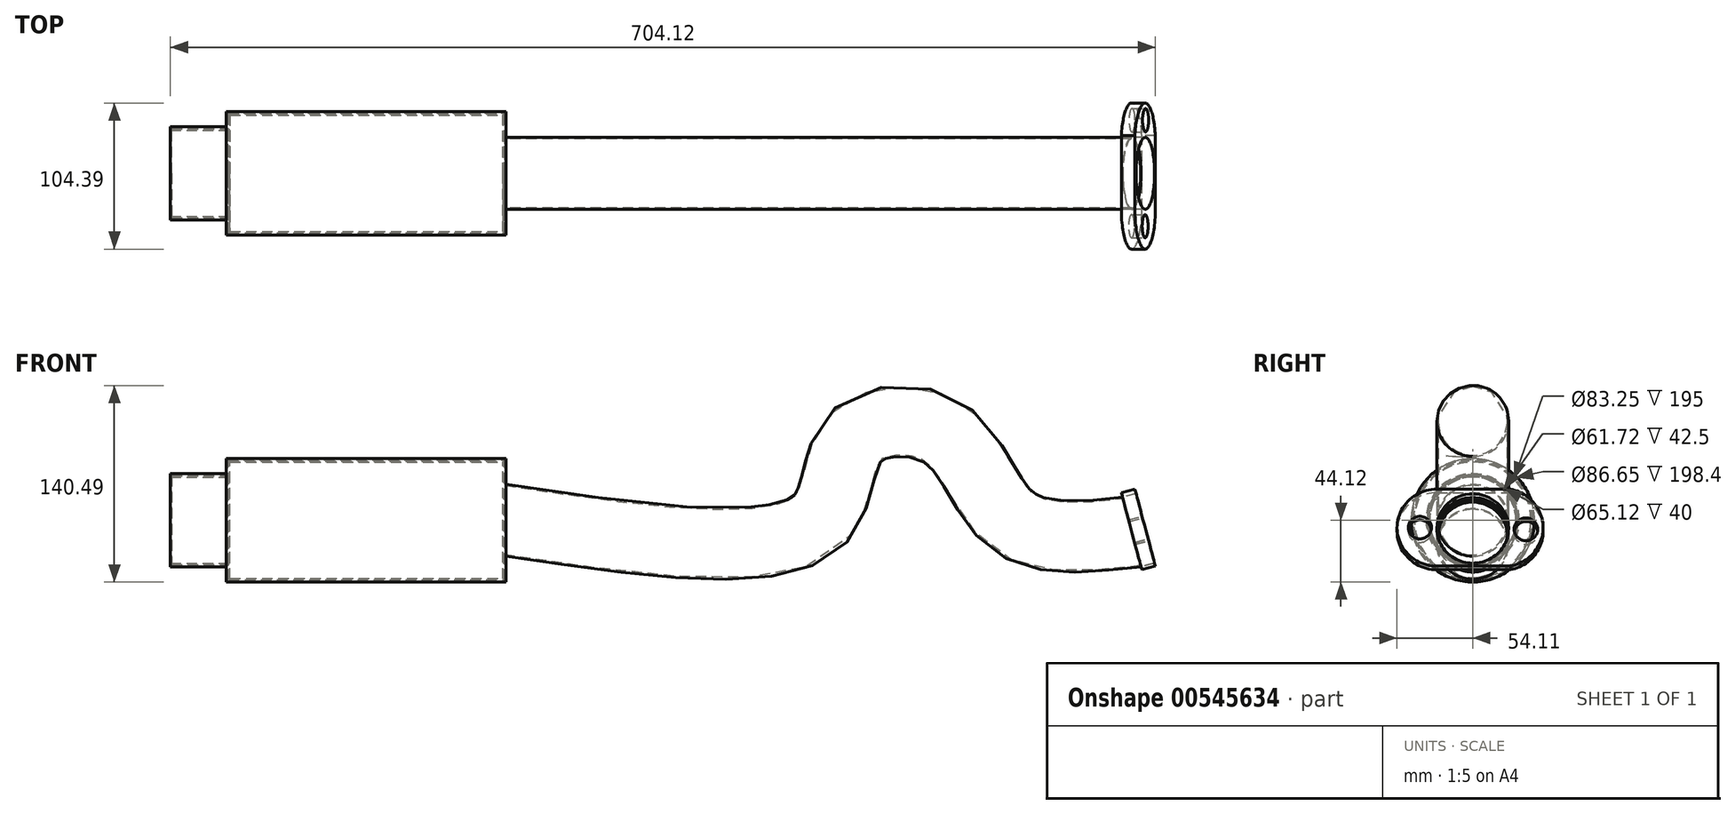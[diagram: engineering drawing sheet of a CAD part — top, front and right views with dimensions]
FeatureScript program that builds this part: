
annotation { "Feature Type Name" : "Feature", "Feature Type Description" : "" }
export const myFeature = defineFeature(function(context is Context, id is Id, definition is map)
    precondition{}
    {
        {
            var Q0;
            Q0=qCreatedBy(makeId("Right.planeOp"),FACE);
            var sketch = newSketch(context, id + "F0", { "sketchPlane" : qUnion([Q0])});
            skCircle(sketch, "E0", {"center": v(0, 0) * mm, "radius": 44.12 * mm});
            skSolve(sketch);
        }
        {
            var Q0;
            Q0=makeQuery(id+"F0.imprint","IMPRINT",FACE,{"disambiguationData":[TD([[makeQuery(id+"F0.imprint","IMPRINT",EDGE,{"derivedFrom":sQuery(id+"F0.wireOp",EDGE,"E0")}),1.0]])]});
            extrude(context, id + "F1", {"entities" : qUnion([Q0]), "oppositeDirection" : true, "depth" : 200 * mm, "offsetDistance" : 25 * mm});
        }
        {
            var Q0;
            Q0=qCreatedBy(makeId("Right.planeOp"),FACE);
            var sketch = newSketch(context, id + "F2", { "sketchPlane" : qUnion([Q0])});
            skCircle(sketch, "E1", {"center": v(0, 0) * mm, "radius": 25.66 * mm});
            skSolve(sketch);
        }
        {
            var Q0;
            Q0=qCreatedBy(makeId("Front.planeOp"),FACE);
            var sketch = newSketch(context, id + "F3", { "sketchPlane" : qUnion([Q0])});
            skFitSpline(sketch, "E2", {"points": [v(0, 0) * mm, v(223.24, 0) * mm, v(249.13, 58.34) * mm, v(312.86, 62.32) * mm, v(361.66, 0) * mm, v(447.3, -8.38) * mm], "startDerivative": vector(954.85, -142.77) * mm, "endDerivative": vector(519.77, 58.14) * mm});
            skSolve(sketch);
        }
        {
            var Q0;
            Q0=makeQuery(id+"F2.imprint","IMPRINT",FACE,{"disambiguationData":[TD([[makeQuery(id+"F2.imprint","IMPRINT",EDGE,{"derivedFrom":sQuery(id+"F2.wireOp",EDGE,"E1")}),1.0]])]});
            var Q1;
            Q1=sQuery(id+"F3.wireOp",EDGE,"E2");
            sweep(context, id + "F4", {"operationType" : NewBodyOperationType.ADD, "profiles" : qUnion([Q0]), "path" : qUnion([Q1])});
        }
        {
            var Q0;
            Q0=makeQuery(id+"F4.opSweep","CAP_FACE",FACE,{"disambiguationData":[OSD([sQuery(id+"F2.wireOp",EDGE,"E1"),sQuery(id+"F3.wireOp",VERTEX,"E2.end")])],"isStart":false});
            var sketch = newSketch(context, id + "F5", { "sketchPlane" : qUnion([Q0])});
            skLineSegment(sketch, "E3.top", {"start": v(-25.63, -93.93) * mm, "end": v(26.97, -93.93) * mm});
            skLineSegment(sketch, "E4.top", {"start": v(-25.63, -150.9) * mm, "end": v(26.97, -150.9) * mm});
            skLineSegment(sketch, "E4.left", {"start": v(-25.63, -121.65) * mm, "end": v(-25.63, -122.41) * mm});
            skArc(sketch, "E5", {"start": v(26.97, -150.9) * mm, "mid": v(50.28, -122.41) * mm, "end": v(26.97, -93.93) * mm});
            skArc(sketch, "E6", {"start": v(-25.63, -93.93) * mm, "mid": v(-54.11, -122.41) * mm, "end": v(-25.63, -150.9) * mm});
            skPoint(sketch, "E3.right.start.orphan", {"position": v(26.97, -121.65) * mm});
            skSolve(sketch);
        }
        {
            var Q0;
            Q0=makeQuery(id+"F5.imprint","IMPRINT",FACE,{"disambiguationData":[TD([[makeQuery(id+"F5.imprint","IMPRINT",EDGE,{"derivedFrom":sQuery(id+"F5.wireOp",EDGE,"E3.top")}),-1.0]])]});
            extrude(context, id + "F6", {"entities" : qUnion([Q0]), "depth" : 10 * mm, "offsetDistance" : 25 * mm});
        }
        {
            var Q0;
            Q0=makeQuery(id+"F6.opExtrude","CAP_FACE",FACE,{"disambiguationData":[OSD([sQuery(id+"F2.wireOp",EDGE,"E1"),sQuery(id+"F3.wireOp",VERTEX,"E2.end"),sQuery(id+"F5.wireOp",EDGE,"E3.top"),sQuery(id+"F5.wireOp",EDGE,"E4.top"),sQuery(id+"F5.wireOp",EDGE,"E5"),sQuery(id+"F5.wireOp",EDGE,"E6")])],"isStart":false});
            var sketch = newSketch(context, id + "F7", { "sketchPlane" : qUnion([Q0])});
            skCircle(sketch, "E7", {"center": v(-37.8, -122.41) * mm, "radius": 8.3 * mm});
            skPoint(sketch, "E7.centerSnap0", {"position": v(-54.11, -122.41) * mm});
            skCircle(sketch, "E8", {"center": v(38.04, -123.67) * mm, "radius": 8.43 * mm});
            skSolve(sketch);
        }
        {
            var Q0;
            Q0=makeQuery(id+"F7.imprint","IMPRINT",FACE,{"disambiguationData":[TD([[makeQuery(id+"F7.imprint","IMPRINT",EDGE,{"derivedFrom":sQuery(id+"F7.wireOp",EDGE,"E7")}),1.0]])]});
            var Q1;
            Q1=makeQuery(id+"F7.imprint","IMPRINT",FACE,{"disambiguationData":[TD([[makeQuery(id+"F7.imprint","IMPRINT",EDGE,{"derivedFrom":sQuery(id+"F7.wireOp",EDGE,"E8")}),1.0]])]});
            extrude(context, id + "F8", {"entities" : qUnion([Q0, Q1]), "operationType" : NewBodyOperationType.REMOVE, "oppositeDirection" : true, "depth" : 25 * mm, "offsetDistance" : 25 * mm});
        }
        {
            var Q0;
            Q0=makeQuery(id+"F1.opExtrude","CAP_FACE",FACE,{"disambiguationData":[OSD([sQuery(id+"F0.wireOp",EDGE,"E0")])],"isStart":false});
            var sketch = newSketch(context, id + "F9", { "sketchPlane" : qUnion([Q0])});
            skCircle(sketch, "E9", {"center": v(0, 0) * mm, "radius": 33.36 * mm});
            skSolve(sketch);
        }
        {
            var Q0;
            Q0=makeQuery(id+"F9.imprint","IMPRINT",FACE,{"disambiguationData":[TD([[makeQuery(id+"F9.imprint","IMPRINT",EDGE,{"derivedFrom":sQuery(id+"F9.wireOp",EDGE,"E9")}),1.0]])]});
            extrude(context, id + "F10", {"entities" : qUnion([Q0]), "operationType" : NewBodyOperationType.ADD, "depth" : 40 * mm, "offsetDistance" : 25 * mm});
        }
        {
            var Q0;
            Q0=makeQuery(id+"F10.opExtrude","CAP_FACE",FACE,{"disambiguationData":[OSD([sQuery(id+"F9.wireOp",EDGE,"E9")])],"isStart":false});
            shell(context, id + "F11", {"entities" : qUnion([Q0]), "thickness" : 2.5 * mm});
        }
        {
            var Q0;
            Q0=makeQuery(id+"F4.opSweep","CAP_FACE",FACE,{"disambiguationData":[OSD([sQuery(id+"F2.wireOp",EDGE,"E1"),sQuery(id+"F3.wireOp",VERTEX,"E2.end")])],"isStart":false});
            shell(context, id + "F12", {"entities" : qUnion([Q0]), "thickness" : 0.8 * mm});
        }
    });
